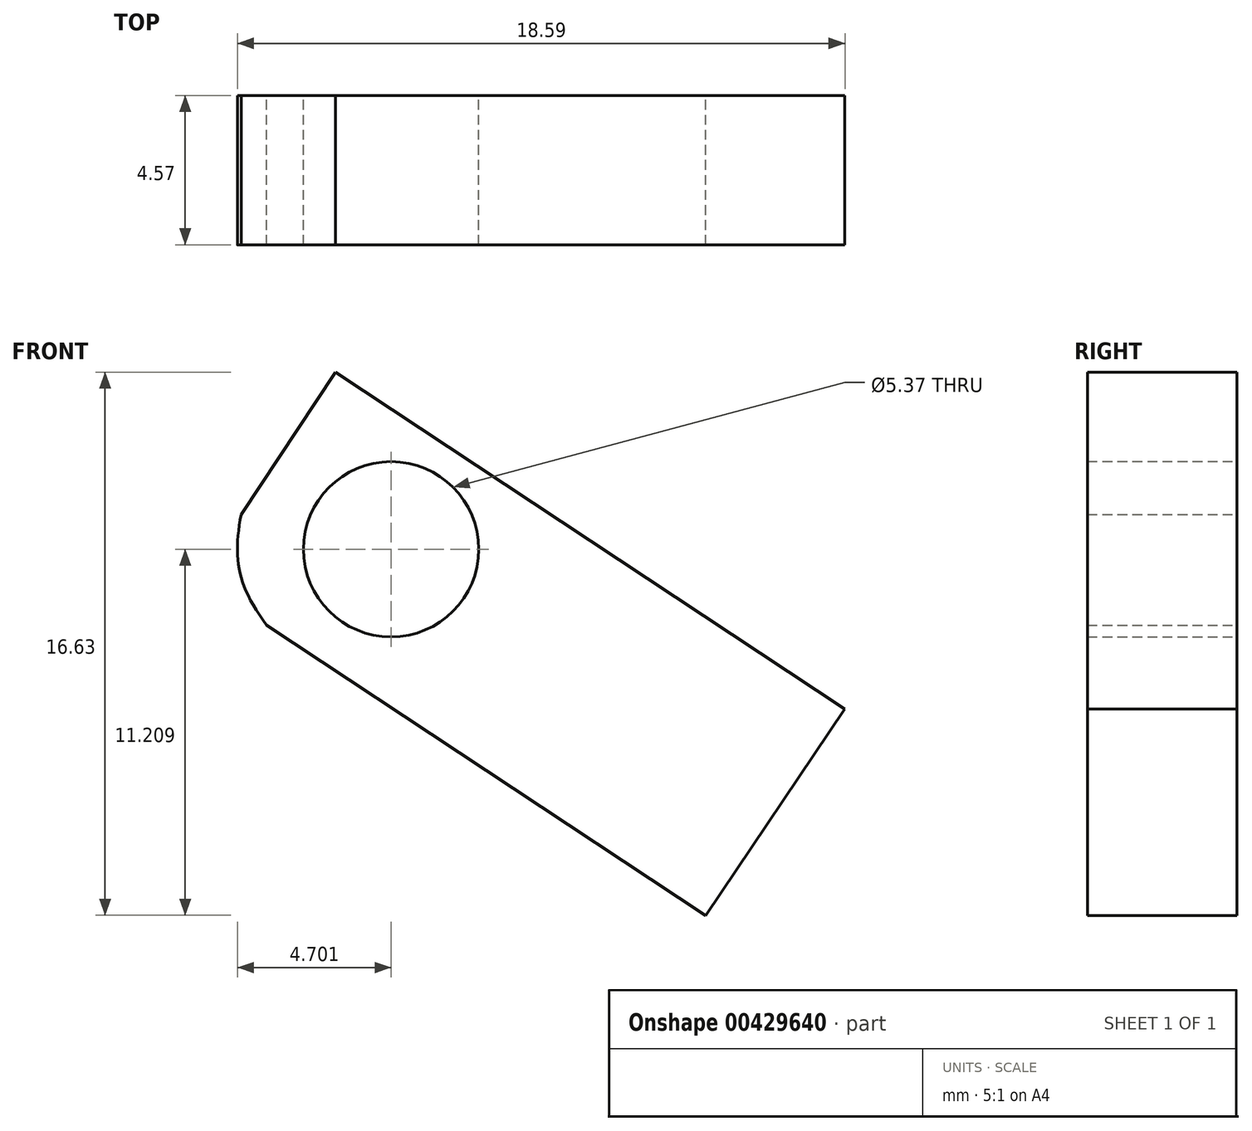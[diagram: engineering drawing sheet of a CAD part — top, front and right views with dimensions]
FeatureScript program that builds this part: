
annotation { "Feature Type Name" : "Feature", "Feature Type Description" : "" }
export const myFeature = defineFeature(function(context is Context, id is Id, definition is map)
    precondition{}
    {
        {
            var Q0;
            Q0=qCreatedBy(makeId("Front.planeOp"),FACE);
            var sketch = newSketch(context, id + "F0", { "sketchPlane" : qUnion([Q0])});
            skLineSegment(sketch, "E0", {"start": v(24.15, -10.56) * mm, "end": v(8.56, -0.24) * mm});
            skLineSegment(sketch, "E1", {"start": v(19.88, -16.87) * mm, "end": v(24.15, -10.56) * mm});
            skPoint(sketch, "E2.1.internal.snap0", {"position": v(6.45, -3.41) * mm});
            skFitSpline(sketch, "E2", {"points": [v(5.67, -4.6) * mm, v(6.45, -7.98) * mm], "startDerivative": vector(-0.74, -4.03) * mm, "endDerivative": vector(2.8, -3.74) * mm});
            skLineSegment(sketch, "E3", {"start": v(5.67, -4.6) * mm, "end": v(8.56, -0.24) * mm});
            skLineSegment(sketch, "E4", {"start": v(6.45, -7.98) * mm, "end": v(19.88, -16.87) * mm});
            skCircle(sketch, "E5", {"center": v(10.26, -5.66) * mm, "radius": 2.68 * mm});
            skSolve(sketch);
        }
        {
            var Q0;
            Q0=makeQuery(id+"F0.imprint","IMPRINT",FACE,{"disambiguationData":[TD([[makeQuery(id+"F0.imprint","IMPRINT",EDGE,{"derivedFrom":sQuery(id+"F0.wireOp",EDGE,"E0")}),1.0]])]});
            extrude(context, id + "F1", {"entities" : qUnion([Q0]), "depth" : 4.57 * mm});
        }
    });
